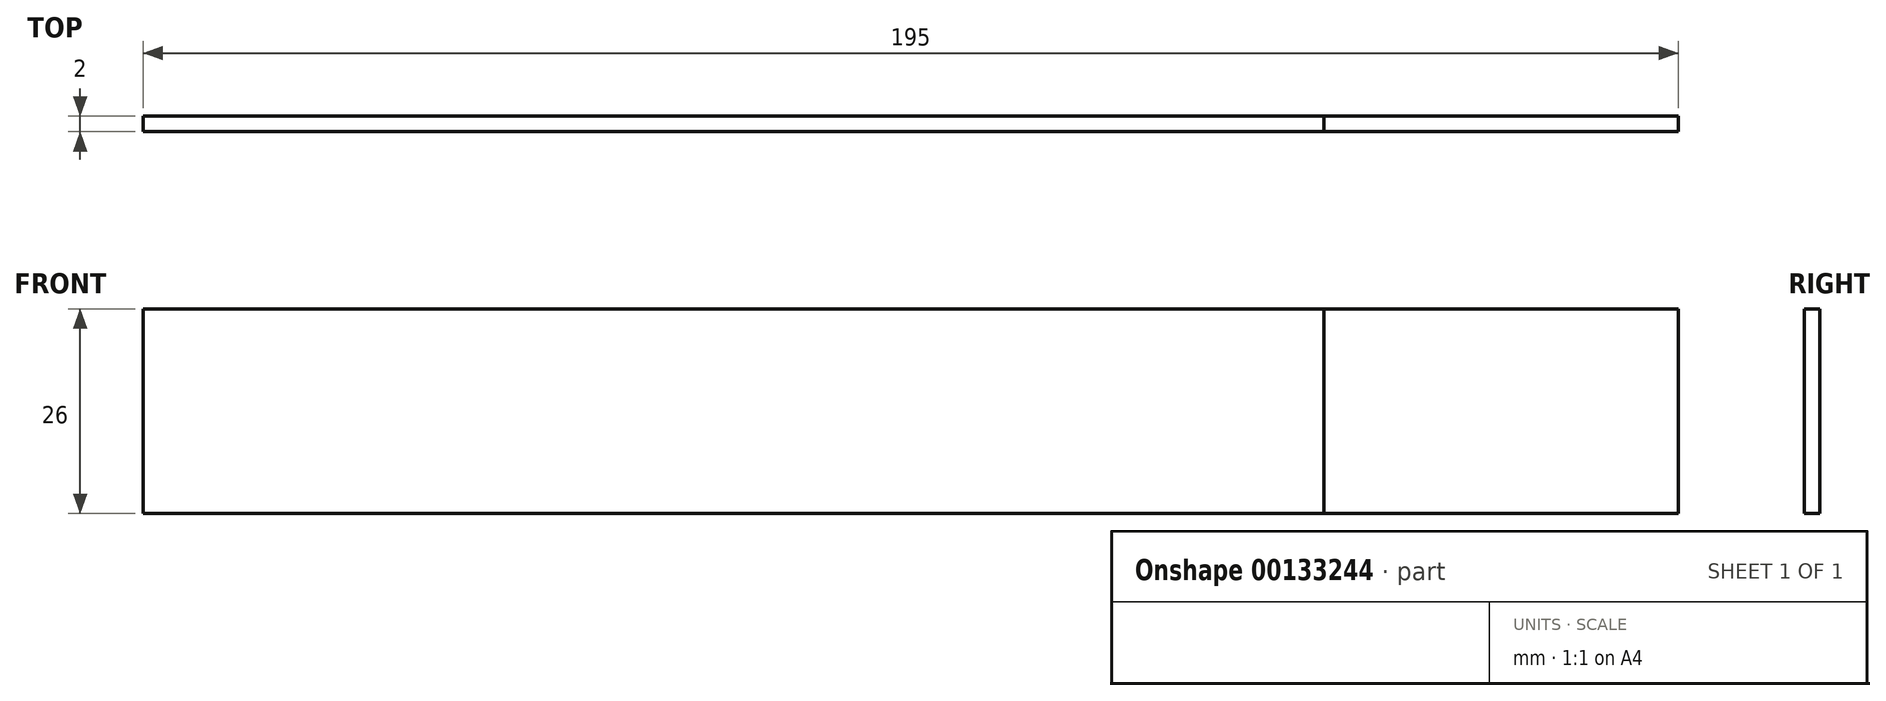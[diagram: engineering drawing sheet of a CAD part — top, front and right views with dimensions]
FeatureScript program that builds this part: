
annotation { "Feature Type Name" : "Feature", "Feature Type Description" : "" }
export const myFeature = defineFeature(function(context is Context, id is Id, definition is map)
    precondition{}
    {
        {
            var Q0;
            Q0=qCreatedBy(makeId("Front.planeOp"),FACE);
            var sketch = newSketch(context, id + "F0", { "sketchPlane" : qUnion([Q0])});
            skLineSegment(sketch, "E0.bottom", {"start": v(-97.5, 0) * mm, "end": v(97.5, 0) * mm});
            skLineSegment(sketch, "E0.top", {"start": v(-97.5, -26) * mm, "end": v(97.5, -26) * mm});
            skLineSegment(sketch, "E0.left", {"start": v(-97.5, 0) * mm, "end": v(-97.5, -26) * mm});
            skLineSegment(sketch, "E0.right", {"start": v(97.5, 0) * mm, "end": v(97.5, -26) * mm});
            skPoint(sketch, "E1", {"position": v(0, 0) * mm});
            skSolve(sketch);
        }
        {
            var Q0;
            Q0 = qSketchRegion(id + "F0", true);
            extrude(context, id + "F1", {"entities" : qUnion([Q0]), "depth" : 2 * mm});
        }
        {
            var Q0;
            Q0=makeQuery(id+"F1.opExtrude","SWEPT_FACE",FACE,{"disambiguationData":[OSD([sQuery(id+"F0.wireOp",EDGE,"E0.left")])]});
            extrude(context, id + "F2", {"entities" : qUnion([Q0]), "oppositeDirection" : true, "depth" : 150 * mm});
        }
        {
            var Q0;
            Q0=makeQuery(id+"F1.opExtrude","SWEPT_FACE",FACE,{"disambiguationData":[OSD([sQuery(id+"F0.wireOp",EDGE,"E0.right")])]});
            var Q1;
            Q1=makeQuery(id+"F2.opExtrude","CAP_FACE",FACE,{"disambiguationData":[OSD([sQuery(id+"F0.wireOp",EDGE,"E0.left")])],"isStart":false});
            extrude(context, id + "F3", {"entities" : qUnion([Q0]), "endBound" : BoundingType.UP_TO_SURFACE, "oppositeDirection" : true, "endBoundEntityFace" : qUnion([Q1]), "depth" : 25 * mm});
        }
    });
